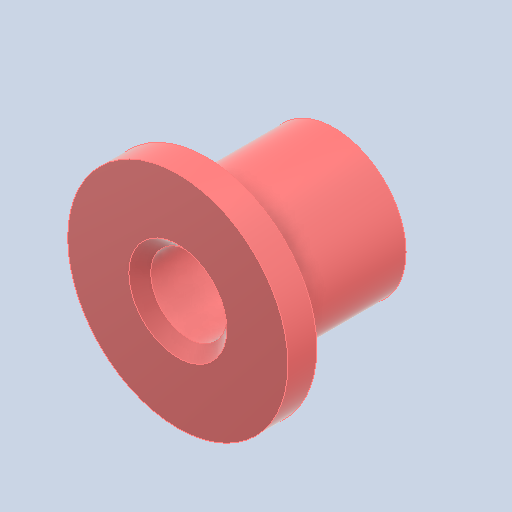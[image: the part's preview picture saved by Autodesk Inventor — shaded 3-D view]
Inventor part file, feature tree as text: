
AUTODESK INVENTOR PART (.ipt)
format: ipt  version: 2022 (Build 260153000, 153)  size: 122,368 bytes
history: native  units: in
note: dims shown in document units (in); Inventor stores cm internally (conversion verified against a paired STEP export)
features: other x3, sketch x2
ambient origin geometry x8: Origin, YZ Plane, XZ Plane, XY Plane, X Axis, Y Axis, Z Axis, Center Point
bodies: Solid1 (feature_tree)
feature tree (5):
  other  "bearingsleeve.ipt"
  other  "Solid1::bearingsleeve.ipt"
  other  "TaggingFeature1"
  sketch  "Sketch1"  dims[d0=0.3937in]
  sketch  "Sketch2"
